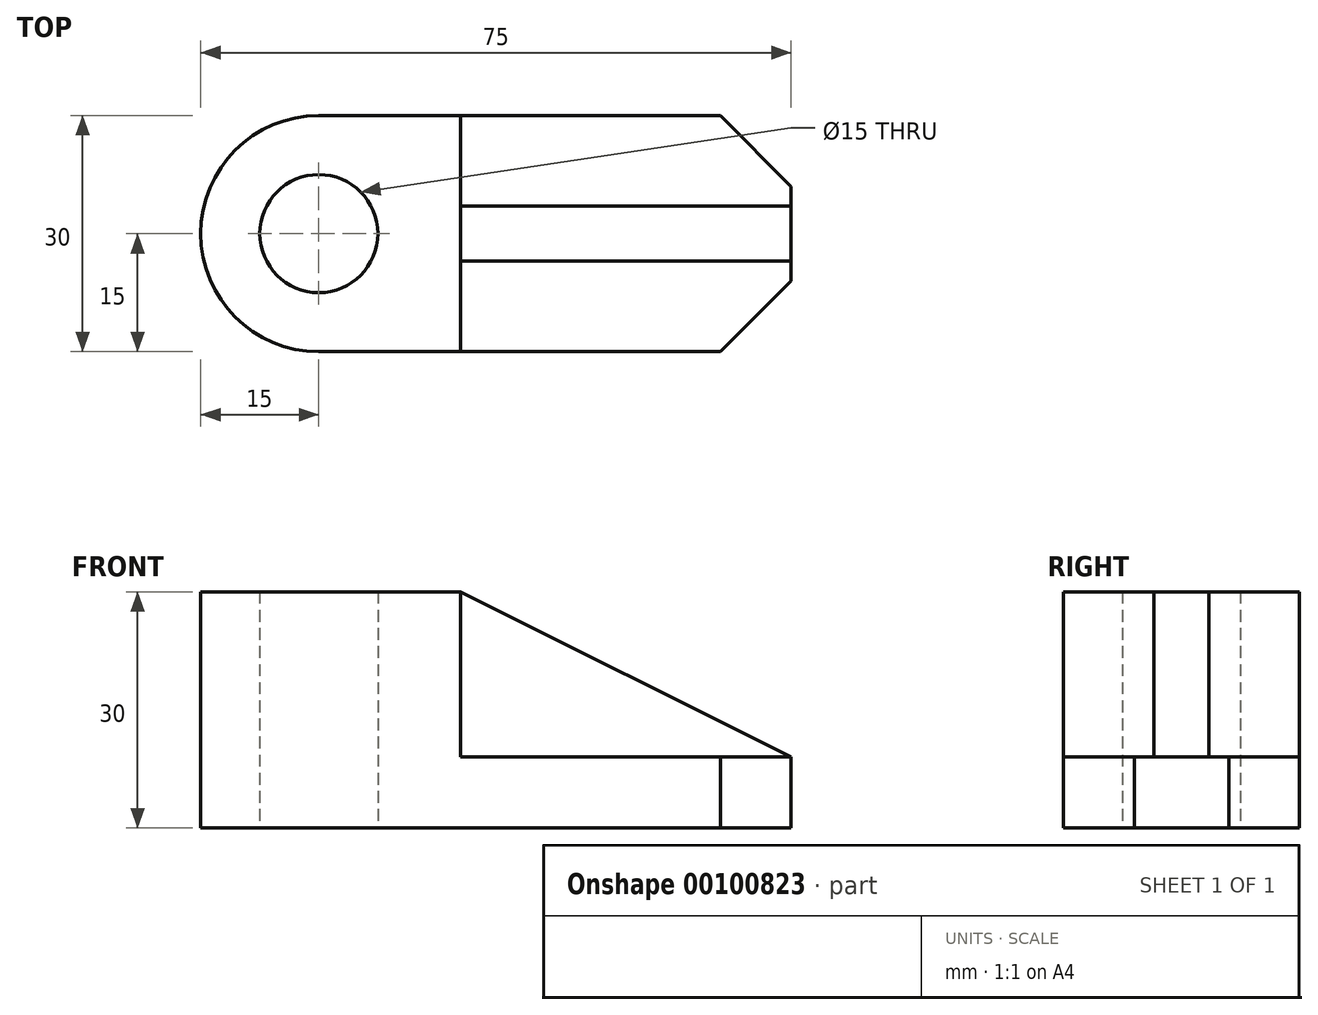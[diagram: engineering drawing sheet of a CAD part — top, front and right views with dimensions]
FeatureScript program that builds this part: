
annotation { "Feature Type Name" : "Feature", "Feature Type Description" : "" }
export const myFeature = defineFeature(function(context is Context, id is Id, definition is map)
    precondition{}
    {
        {
            var Q0;
            Q0=qCreatedBy(makeId("Top.planeOp"),FACE);
            var sketch = newSketch(context, id + "F0", { "sketchPlane" : qUnion([Q0])});
            skLineSegment(sketch, "E0.bottom", {"start": v(0, 0) * mm, "end": v(51, 0) * mm});
            skLineSegment(sketch, "E0.top", {"start": v(0, 30) * mm, "end": v(51, 30) * mm});
            skArc(sketch, "E1", {"start": v(0, 30) * mm, "mid": v(-15, 15) * mm, "end": v(0, 0) * mm});
            skLineSegment(sketch, "E2", {"start": v(51, 30) * mm, "end": v(60, 21) * mm});
            skLineSegment(sketch, "E3", {"start": v(60, 21) * mm, "end": v(60, 9) * mm});
            skLineSegment(sketch, "E4", {"start": v(60, 9) * mm, "end": v(51, 0) * mm});
            skCircle(sketch, "E5", {"center": v(0, 15) * mm, "radius": 7.5 * mm});
            skSolve(sketch);
        }
        {
            var Q0;
            Q0=makeQuery(id+"F0.imprint","IMPRINT",FACE,{"disambiguationData":[TD([[makeQuery(id+"F0.imprint","IMPRINT",EDGE,{"derivedFrom":sQuery(id+"F0.wireOp",EDGE,"E0.bottom")}),1.0]])]});
            extrude(context, id + "F1", {"entities" : qUnion([Q0]), "depth" : 9 * mm});
        }
        {
            var Q0;
            Q0=makeQuery(id+"F1.opExtrude","CAP_FACE",FACE,{"disambiguationData":[OSD([sQuery(id+"F0.wireOp",EDGE,"E0.bottom"),sQuery(id+"F0.wireOp",EDGE,"E0.top"),sQuery(id+"F0.wireOp",EDGE,"E1"),sQuery(id+"F0.wireOp",EDGE,"E2"),sQuery(id+"F0.wireOp",EDGE,"E3"),sQuery(id+"F0.wireOp",EDGE,"E4"),sQuery(id+"F0.wireOp",EDGE,"E5")])],"isStart":false});
            var sketch = newSketch(context, id + "F2", { "sketchPlane" : qUnion([Q0])});
            skLineSegment(sketch, "E6", {"start": v(18, 30) * mm, "end": v(18, 0) * mm});
            skSolve(sketch);
        }
        {
            var Q0;
            {var subQ2=sQuery(id+"F2.wireOp",EDGE,"E6");Q0=makeQuery(id+"F2.imprint","IMPRINT",FACE,{"disambiguationData":[TD([[makeQuery(id+"F2.imprint","IMPRINT",EDGE,{"derivedFrom":subQ2}),-1.0]])]});}
            extrude(context, id + "F3", {"entities" : qUnion([Q0]), "operationType" : NewBodyOperationType.ADD, "depth" : 21 * mm});
        }
        {
            var Q0;
            Q0=qCreatedBy(makeId("Front.planeOp"),FACE);
            cPlane(context, id + "F4", {"entities" : qUnion([Q0]), "cplaneType" : CPlaneType.OFFSET, "offset" : 15 * mm, "oppositeDirection" : true, "width" : 150 * mm, "height" : 150 * mm});
        }
        {
            var Q0;
            Q0=qCreatedBy(id+"F4.planeOp",FACE);
            var sketch = newSketch(context, id + "F5", { "sketchPlane" : qUnion([Q0])});
            skPoint(sketch, "E7.0", {"position": v(18, 30) * mm});
            skPoint(sketch, "E8.0", {"position": v(18, 9) * mm});
            skPoint(sketch, "E9.0", {"position": v(60, 9) * mm});
            skLineSegment(sketch, "E10", {"start": v(18, 30) * mm, "end": v(60, 9) * mm});
            skLineSegment(sketch, "E11", {"start": v(18, 30) * mm, "end": v(18, 9) * mm});
            skLineSegment(sketch, "E12.0", {"start": v(18, 9) * mm, "end": v(51, 9) * mm});
            skLineSegment(sketch, "E13.0", {"start": v(60, 9) * mm, "end": v(51, 9) * mm});
            skSolve(sketch);
        }
        {
            var Q0;
            Q0=makeQuery(id+"F5.imprint","IMPRINT",FACE,{"disambiguationData":[TD([[makeQuery(id+"F5.imprint","IMPRINT",EDGE,{"derivedFrom":sQuery(id+"F5.wireOp",EDGE,"E10")}),-1.0]])]});
            extrude(context, id + "F6", {"entities" : qUnion([Q0]), "operationType" : NewBodyOperationType.ADD, "endBound" : BoundingType.SYMMETRIC, "depth" : 7 * mm});
        }
    });
